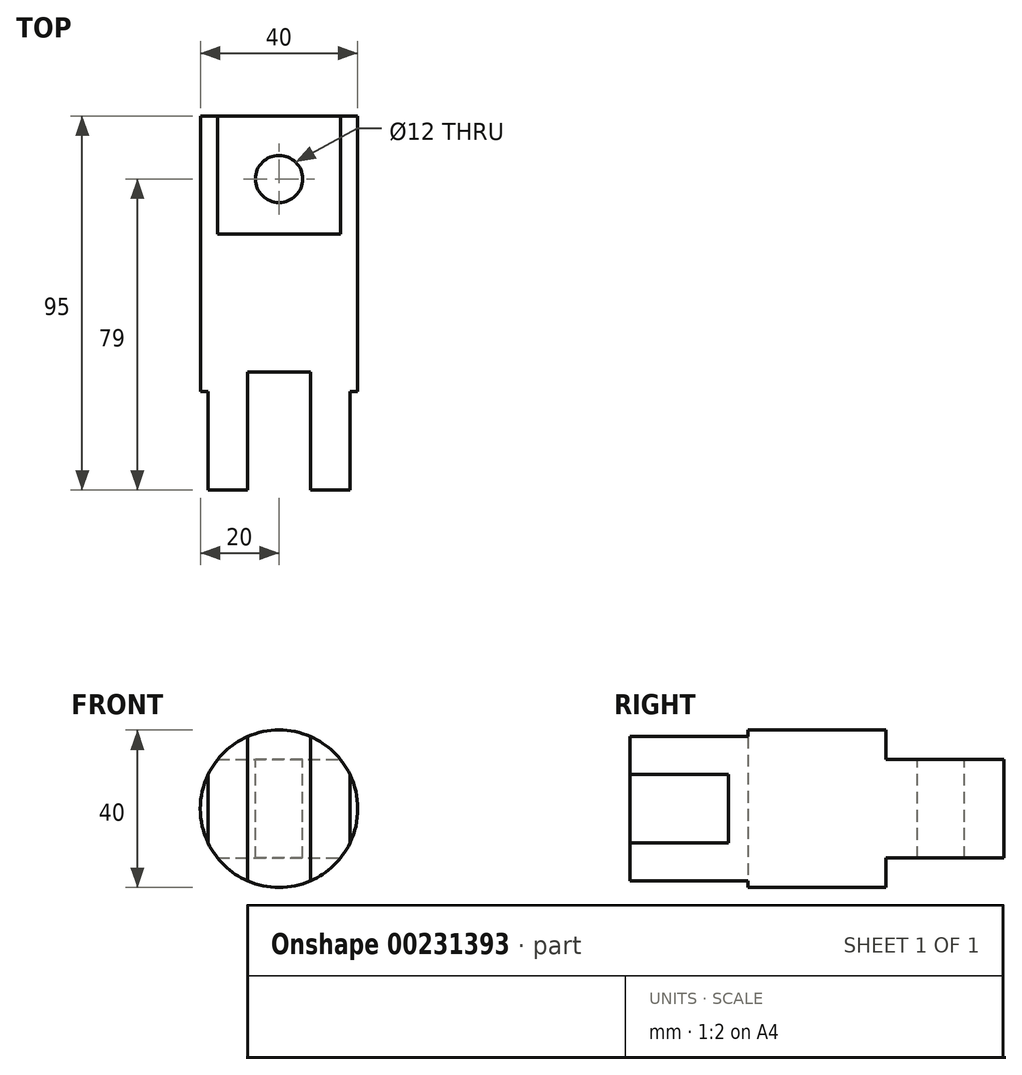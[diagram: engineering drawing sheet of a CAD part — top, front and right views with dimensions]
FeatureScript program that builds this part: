
annotation { "Feature Type Name" : "Feature", "Feature Type Description" : "" }
export const myFeature = defineFeature(function(context is Context, id is Id, definition is map)
    precondition{}
    {
        {
            var Q0;
            Q0=qCreatedBy(makeId("Front.planeOp"),FACE);
            var sketch = newSketch(context, id + "F0", { "sketchPlane" : qUnion([Q0])});
            skCircle(sketch, "E0", {"center": v(0, 0) * mm, "radius": 20 * mm});
            skSolve(sketch);
        }
        {
            var Q0;
            Q0=makeQuery(id+"F0.imprint","IMPRINT",FACE,{"disambiguationData":[TD([[makeQuery(id+"F0.imprint","IMPRINT",EDGE,{"derivedFrom":sQuery(id+"F0.wireOp",EDGE,"E0")}),1.0]])]});
            extrude(context, id + "F1", {"entities" : qUnion([Q0]), "endBound" : BoundingType.SYMMETRIC, "depth" : 95 * mm});
        }
        {
            var Q0;
            Q0=makeQuery(id+"F1.opExtrude","CAP_FACE",FACE,{"disambiguationData":[OSD([sQuery(id+"F0.wireOp",EDGE,"E0")])],"isStart":false});
            var sketch = newSketch(context, id + "F2", { "sketchPlane" : qUnion([Q0])});
            skLineSegment(sketch, "E1", {"start": v(-8, 18.33) * mm, "end": v(-8, -18.33) * mm});
            skLineSegment(sketch, "E2.MirrorCS", {"start": v(8, 18.33) * mm, "end": v(8, -18.33) * mm});
            skCircle(sketch, "E3.0", {"center": v(0, 0) * mm, "radius": 20 * mm});
            skSolve(sketch);
        }
        {
            var Q0;
            {var subQ0=sQuery(id+"F2.wireOp",EDGE,"E1");Q0=makeQuery(id+"F2.imprint","IMPRINT",FACE,{"disambiguationData":[TD([[makeQuery(id+"F2.imprint","IMPRINT",EDGE,{"derivedFrom":subQ0}),1.0]])]});}
            extrude(context, id + "F3", {"entities" : qUnion([Q0]), "operationType" : NewBodyOperationType.REMOVE, "oppositeDirection" : true, "depth" : 30 * mm});
        }
        {
            var Q0;
            {var subQ0=sQuery(id+"F2.wireOp",EDGE,"E2.MirrorCS");Q0=makeQuery(id+"F2.imprint","IMPRINT",FACE,{"disambiguationData":[TD([[makeQuery(id+"F2.imprint","IMPRINT",EDGE,{"derivedFrom":subQ0}),1.0]])]});}
            var sketch = newSketch(context, id + "F4", { "sketchPlane" : qUnion([Q0])});
            skLineSegment(sketch, "E4", {"start": v(18, 8.72) * mm, "end": v(18, -8.72) * mm});
            skCircle(sketch, "E5.0", {"center": v(0, 0) * mm, "radius": 20 * mm});
            skLineSegment(sketch, "E6.MirrorCS", {"start": v(-18, 8.72) * mm, "end": v(-18, -8.72) * mm});
            skSolve(sketch);
        }
        {
            var Q0;
            {var subQ0=sQuery(id+"F4.wireOp",EDGE,"E6.MirrorCS");Q0=makeQuery(id+"F4.imprint","IMPRINT",FACE,{"disambiguationData":[TD([[makeQuery(id+"F4.imprint","IMPRINT",EDGE,{"derivedFrom":subQ0}),-1.0]])]});}
            var Q1;
            {var subQ0=sQuery(id+"F4.wireOp",EDGE,"E4");Q1=makeQuery(id+"F4.imprint","IMPRINT",FACE,{"disambiguationData":[TD([[makeQuery(id+"F4.imprint","IMPRINT",EDGE,{"derivedFrom":subQ0}),1.0]])]});}
            extrude(context, id + "F5", {"entities" : qUnion([Q0, Q1]), "operationType" : NewBodyOperationType.REMOVE, "oppositeDirection" : true, "depth" : 25 * mm});
        }
        {
            var Q0;
            Q0=makeQuery(id+"F1.opExtrude","CAP_FACE",FACE,{"disambiguationData":[OSD([sQuery(id+"F0.wireOp",EDGE,"E0")])],"isStart":true});
            var sketch = newSketch(context, id + "F6", { "sketchPlane" : qUnion([Q0])});
            skLineSegment(sketch, "E7", {"start": v(15.61, 12.5) * mm, "end": v(-15.61, 12.5) * mm});
            skLineSegment(sketch, "E8", {"start": v(15.61, -12.5) * mm, "end": v(-15.61, -12.5) * mm});
            skCircle(sketch, "E9.0", {"center": v(0, 0) * mm, "radius": 20 * mm});
            skSolve(sketch);
        }
        {
            var Q0;
            {var subQ0=sQuery(id+"F6.wireOp",EDGE,"E7");Q0=makeQuery(id+"F6.imprint","IMPRINT",FACE,{"disambiguationData":[TD([[makeQuery(id+"F6.imprint","IMPRINT",EDGE,{"derivedFrom":subQ0}),-1.0]])]});}
            var Q1;
            {var subQ0=sQuery(id+"F6.wireOp",EDGE,"E8");Q1=makeQuery(id+"F6.imprint","IMPRINT",FACE,{"disambiguationData":[TD([[makeQuery(id+"F6.imprint","IMPRINT",EDGE,{"derivedFrom":subQ0}),1.0]])]});}
            extrude(context, id + "F7", {"entities" : qUnion([Q0, Q1]), "operationType" : NewBodyOperationType.REMOVE, "oppositeDirection" : true, "depth" : 30 * mm});
        }
        {
            var Q0;
            Q0=makeQuery(id+"F7.boolean.opBoolean","COPY",FACE,{"derivedFrom":makeQuery(id+"F7.opExtrude","SWEPT_FACE",FACE,{"disambiguationData":[OSD([sQuery(id+"F6.wireOp",EDGE,"E7")])]})});
            var sketch = newSketch(context, id + "F8", { "sketchPlane" : qUnion([Q0])});
            skCircle(sketch, "E10", {"center": v(0, 31.5) * mm, "radius": 6 * mm});
            skSolve(sketch);
        }
        {
            var Q0;
            Q0=qSketchRegion(id+"F8",true);
            extrude(context, id + "F9", {"entities" : qUnion([Q0]), "operationType" : NewBodyOperationType.ADD, "depth" : 25 * mm});
        }
        {
            var Q0;
            Q0=makeQuery(id+"F9.opExtrude","CAP_FACE",FACE,{"disambiguationData":[OSD([sQuery(id+"F8.wireOp",EDGE,"E10")])],"isStart":false});
            extrude(context, id + "F10", {"entities" : qUnion([Q0]), "operationType" : NewBodyOperationType.REMOVE, "endBound" : BoundingType.THROUGH_ALL, "oppositeDirection" : true, "depth" : 25 * mm});
        }
    });
